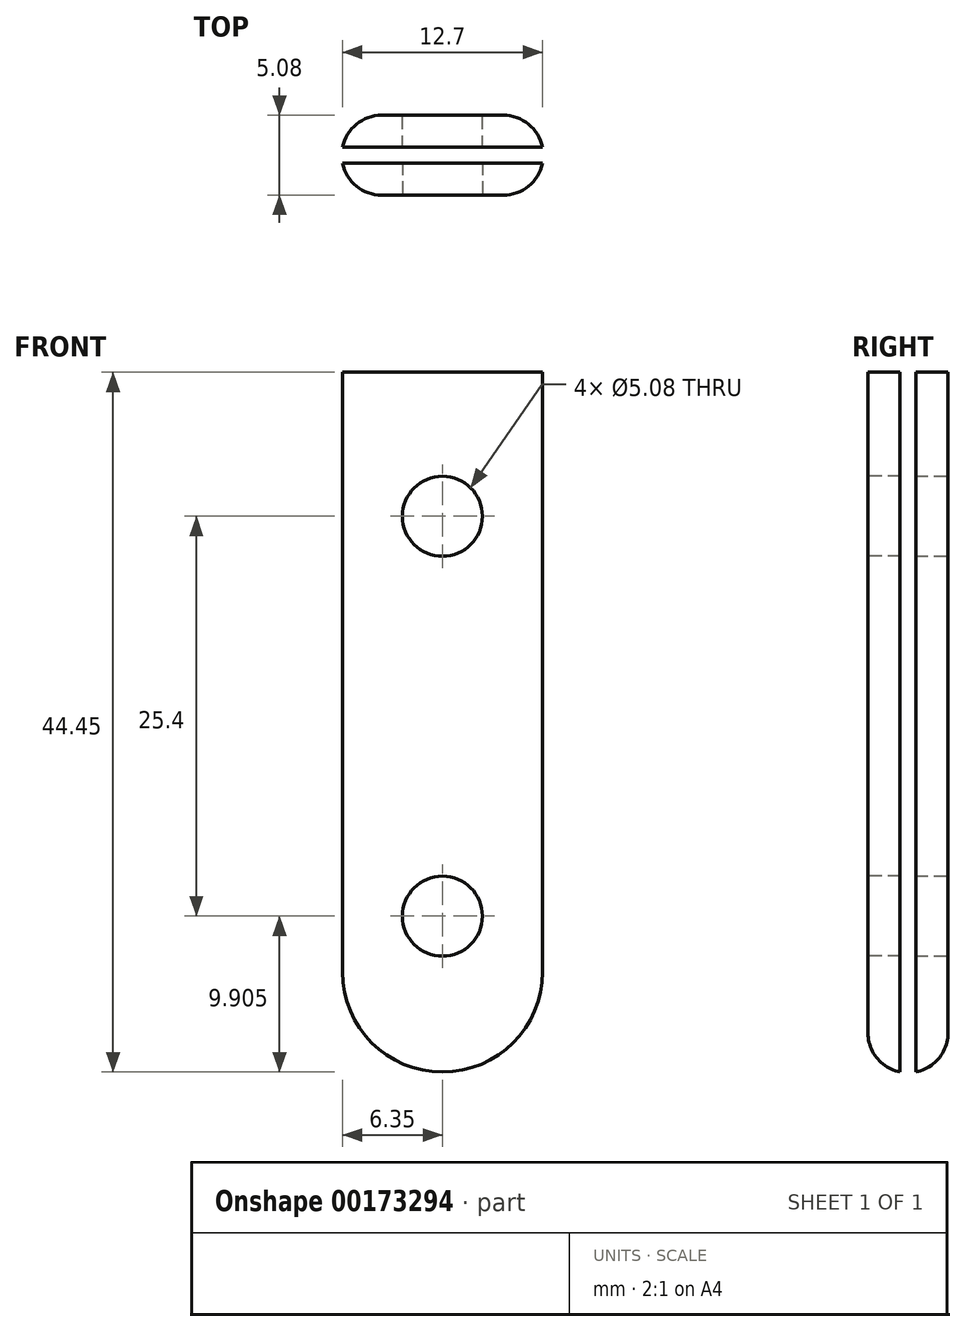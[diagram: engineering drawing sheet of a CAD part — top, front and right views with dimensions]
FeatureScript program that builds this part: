
annotation { "Feature Type Name" : "Feature", "Feature Type Description" : "" }
export const myFeature = defineFeature(function(context is Context, id is Id, definition is map)
    precondition{}
    {
        {
            var Q0;
            Q0=qCreatedBy(makeId("Front.planeOp"),FACE);
            var sketch = newSketch(context, id + "F0", { "sketchPlane" : qUnion([Q0])});
            skLineSegment(sketch, "E0.bottom", {"start": v(0, 25.04) * mm, "end": v(12.7, 25.04) * mm});
            skLineSegment(sketch, "E0.top", {"start": v(6.35, -19.41) * mm, "end": v(6.35, -19.41) * mm});
            skLineSegment(sketch, "E0.left", {"start": v(0, 25.04) * mm, "end": v(0, -13.06) * mm});
            skLineSegment(sketch, "E0.right", {"start": v(12.7, 25.04) * mm, "end": v(12.7, -13.06) * mm});
            skPoint(sketch, "E1.visualSharp", {"position": v(0, -19.41) * mm});
            skArc(sketch, "E1.filletArc", {"start": v(0, -13.06) * mm, "mid": v(1.86, -17.55) * mm, "end": v(6.35, -19.41) * mm});
            skPoint(sketch, "E2.visualSharp", {"position": v(12.7, -19.41) * mm});
            skArc(sketch, "E2.filletArc", {"start": v(6.35, -19.41) * mm, "mid": v(10.84, -17.55) * mm, "end": v(12.7, -13.06) * mm});
            skSolve(sketch);
        }
        {
            var Q0;
            Q0=makeQuery(id+"F0.imprint","IMPRINT",FACE,{"disambiguationData":[TD([[makeQuery(id+"F0.imprint","IMPRINT",EDGE,{"derivedFrom":sQuery(id+"F0.wireOp",EDGE,"E0.bottom")}),-1.0]])]});
            extrude(context, id + "F1", {"entities" : qUnion([Q0]), "depth" : 2.03 * mm});
        }
        {
            var Q0;
            Q0=makeQuery(id+"F1.opExtrude","CAP_FACE",FACE,{"disambiguationData":[OSD([sQuery(id+"F0.wireOp",EDGE,"E0.bottom"),sQuery(id+"F0.wireOp",EDGE,"E0.left"),sQuery(id+"F0.wireOp",EDGE,"E0.right"),sQuery(id+"F0.wireOp",EDGE,"E1.filletArc"),sQuery(id+"F0.wireOp",EDGE,"E2.filletArc")])],"isStart":false});
            var sketch = newSketch(context, id + "F2", { "sketchPlane" : qUnion([Q0])});
            skCircle(sketch, "E3", {"center": v(6.35, 15.9) * mm, "radius": 2.54 * mm});
            skCircle(sketch, "E4", {"center": v(6.35, -9.5) * mm, "radius": 2.54 * mm});
            skSolve(sketch);
        }
        {
            var Q0;
            Q0=makeQuery(id+"F2.imprint","IMPRINT",FACE,{"disambiguationData":[TD([[makeQuery(id+"F2.imprint","IMPRINT",EDGE,{"derivedFrom":sQuery(id+"F2.wireOp",EDGE,"E4")}),1.0]])]});
            var Q1;
            Q1=makeQuery(id+"F2.imprint","IMPRINT",FACE,{"disambiguationData":[TD([[makeQuery(id+"F2.imprint","IMPRINT",EDGE,{"derivedFrom":sQuery(id+"F2.wireOp",EDGE,"E3")}),1.0]])]});
            extrude(context, id + "F3", {"entities" : qUnion([Q0, Q1]), "operationType" : NewBodyOperationType.REMOVE, "oppositeDirection" : true, "depth" : 2.03 * mm});
        }
        {
            var Q0;
            Q0=makeQuery(id+"F1.opExtrude","CAP_EDGE",EDGE,{"disambiguationData":[OSD([sQuery(id+"F0.wireOp",EDGE,"E0.right")])],"isStart":false});
            fillet(context, id + "F4", {"entities" : qUnion([Q0]), "radius" : 2.54 * mm, "tangentPropagation" : true, "allowEdgeOverflow" : false});
        }
        {
            var Q0;
            Q0=makeQuery(id+"F1.opExtrude","CAP_FACE",FACE,{"disambiguationData":[OSD([sQuery(id+"F0.wireOp",EDGE,"E0.bottom"),sQuery(id+"F0.wireOp",EDGE,"E0.left"),sQuery(id+"F0.wireOp",EDGE,"E0.right"),sQuery(id+"F0.wireOp",EDGE,"E1.filletArc"),sQuery(id+"F0.wireOp",EDGE,"E2.filletArc")])],"isStart":true});
            cPlane(context, id + "F5", {"entities" : qUnion([Q0]), "cplaneType" : CPlaneType.OFFSET, "offset" : 0.5 * mm, "width" : 152.4 * mm, "height" : 152.4 * mm});
        }
        {
            var Q0;
            Q0=makeQuery(id+"F1.opExtrude","SWEPT_BODY",BODY,{"disambiguationData":[OSD([sQuery(id+"F0.wireOp",EDGE,"E0.bottom"),sQuery(id+"F0.wireOp",EDGE,"E0.left"),sQuery(id+"F0.wireOp",EDGE,"E0.right"),sQuery(id+"F0.wireOp",EDGE,"E1.filletArc"),sQuery(id+"F0.wireOp",EDGE,"E2.filletArc")])]});
            var Q1;
            Q1=qCreatedBy(id+"F5.planeOp",FACE);
            mirror(context, id + "F6", {"entities" : qUnion([Q0]), "mirrorPlane" : qUnion([Q1])});
        }
    });
